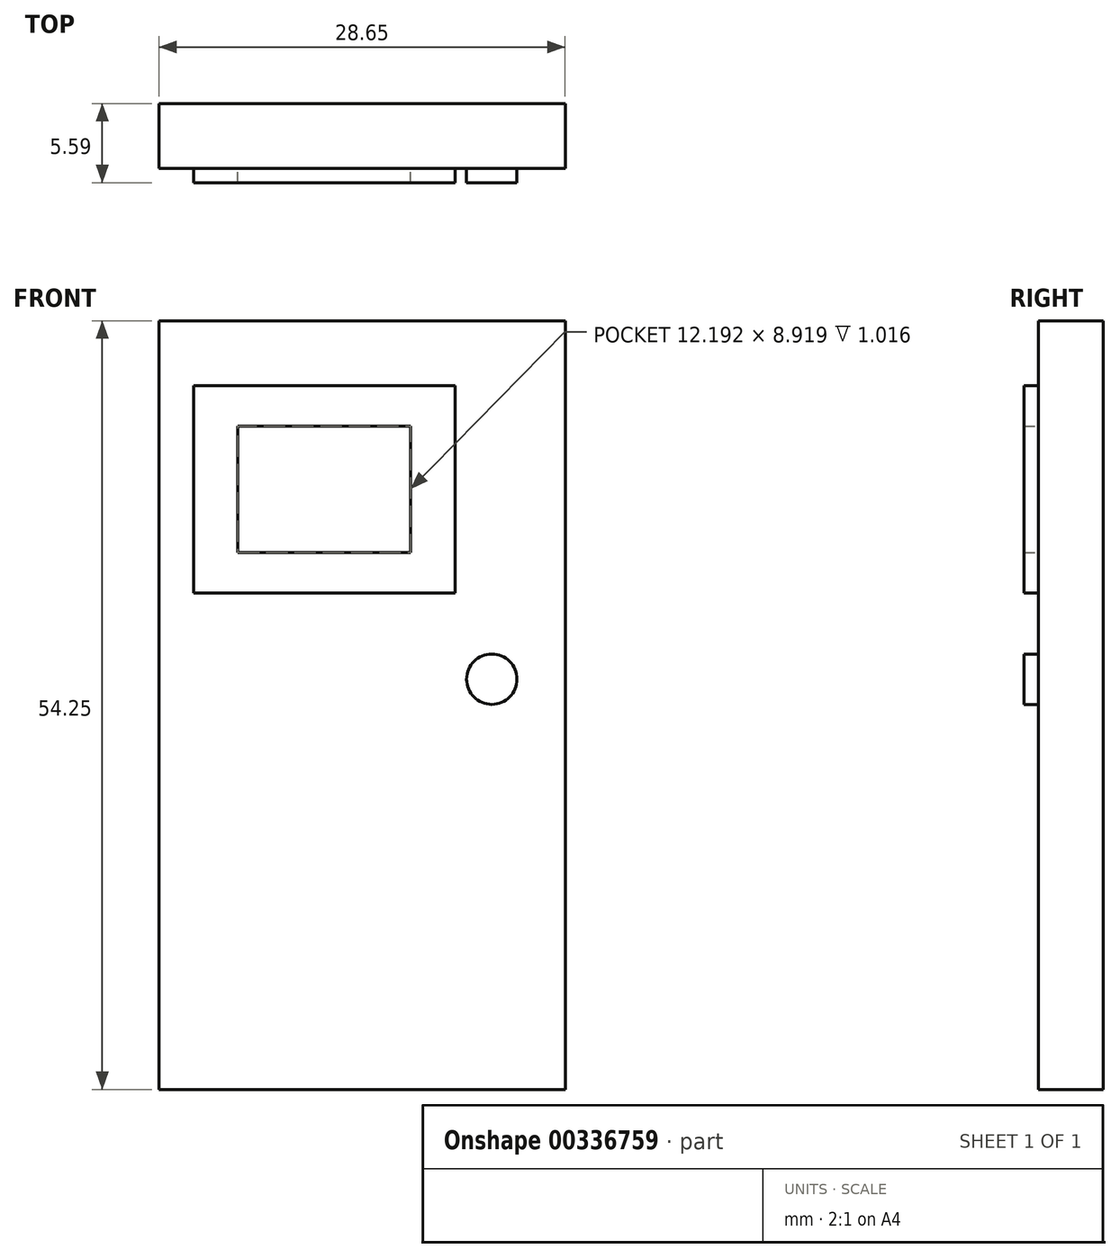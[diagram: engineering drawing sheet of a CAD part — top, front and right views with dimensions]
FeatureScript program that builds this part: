
annotation { "Feature Type Name" : "Feature", "Feature Type Description" : "" }
export const myFeature = defineFeature(function(context is Context, id is Id, definition is map)
    precondition{}
    {
        {
            var Q0;
            Q0=qCreatedBy(makeId("Front.planeOp"),FACE);
            var sketch = newSketch(context, id + "F0", { "sketchPlane" : qUnion([Q0])});
            skLineSegment(sketch, "E0", {"start": v(-34.75, 20.57) * mm, "end": v(-34.75, -33.68) * mm});
            skLineSegment(sketch, "E1", {"start": v(-34.75, -33.68) * mm, "end": v(-6.1, -33.68) * mm});
            skLineSegment(sketch, "E2", {"start": v(-6.1, -33.68) * mm, "end": v(-6.1, 20.57) * mm});
            skLineSegment(sketch, "E3", {"start": v(-6.1, 20.57) * mm, "end": v(-34.75, 20.57) * mm});
            skSolve(sketch);
        }
        {
            var Q0;
            Q0 = qSketchRegion(id + "F0", true);
            extrude(context, id + "F1", {"entities" : qUnion([Q0]), "depth" : 4.57 * mm});
        }
        {
            var Q0;
            Q0=makeQuery(id+"F1.opExtrude","CAP_FACE",FACE,{"disambiguationData":[OSD([sQuery(id+"F0.wireOp",EDGE,"E0"),sQuery(id+"F0.wireOp",EDGE,"E1"),sQuery(id+"F0.wireOp",EDGE,"E2"),sQuery(id+"F0.wireOp",EDGE,"E3")])],"isStart":false});
            var sketch = newSketch(context, id + "F2", { "sketchPlane" : qUnion([Q0])});
            skCircle(sketch, "E4", {"center": v(-11.28, -4.72) * mm, "radius": 1.78 * mm});
            skLineSegment(sketch, "E5", {"start": v(-29.18, 13.15) * mm, "end": v(-29.18, 4.23) * mm});
            skLineSegment(sketch, "E6", {"start": v(-29.18, 4.23) * mm, "end": v(-17, 4.23) * mm});
            skLineSegment(sketch, "E7", {"start": v(-17, 4.23) * mm, "end": v(-17, 13.15) * mm});
            skLineSegment(sketch, "E8", {"start": v(-17, 13.15) * mm, "end": v(-29.18, 13.15) * mm});
            skLineSegment(sketch, "E9", {"start": v(-23.09, 13.15) * mm, "end": v(-23.09, 4.23) * mm});
            skLineSegment(sketch, "E10", {"start": v(-29.18, 8.69) * mm, "end": v(-17, 8.69) * mm});
            skLineSegment(sketch, "E11.bottom", {"start": v(-32.3, 16) * mm, "end": v(-13.87, 16) * mm});
            skLineSegment(sketch, "E11.top", {"start": v(-32.3, 1.37) * mm, "end": v(-13.87, 1.37) * mm});
            skLineSegment(sketch, "E11.left", {"start": v(-32.3, 16) * mm, "end": v(-32.3, 1.37) * mm});
            skLineSegment(sketch, "E11.right", {"start": v(-13.87, 16) * mm, "end": v(-13.87, 1.37) * mm});
            skPoint(sketch, "E11.middle", {"position": v(-23.09, 8.69) * mm});
            skSolve(sketch);
        }
        {
            var Q0;
            Q0 = qSketchRegion(id + "F2", true);
            extrude(context, id + "F3", {"entities" : qUnion([Q0]), "operationType" : NewBodyOperationType.ADD, "depth" : 1.02 * mm});
        }
    });
